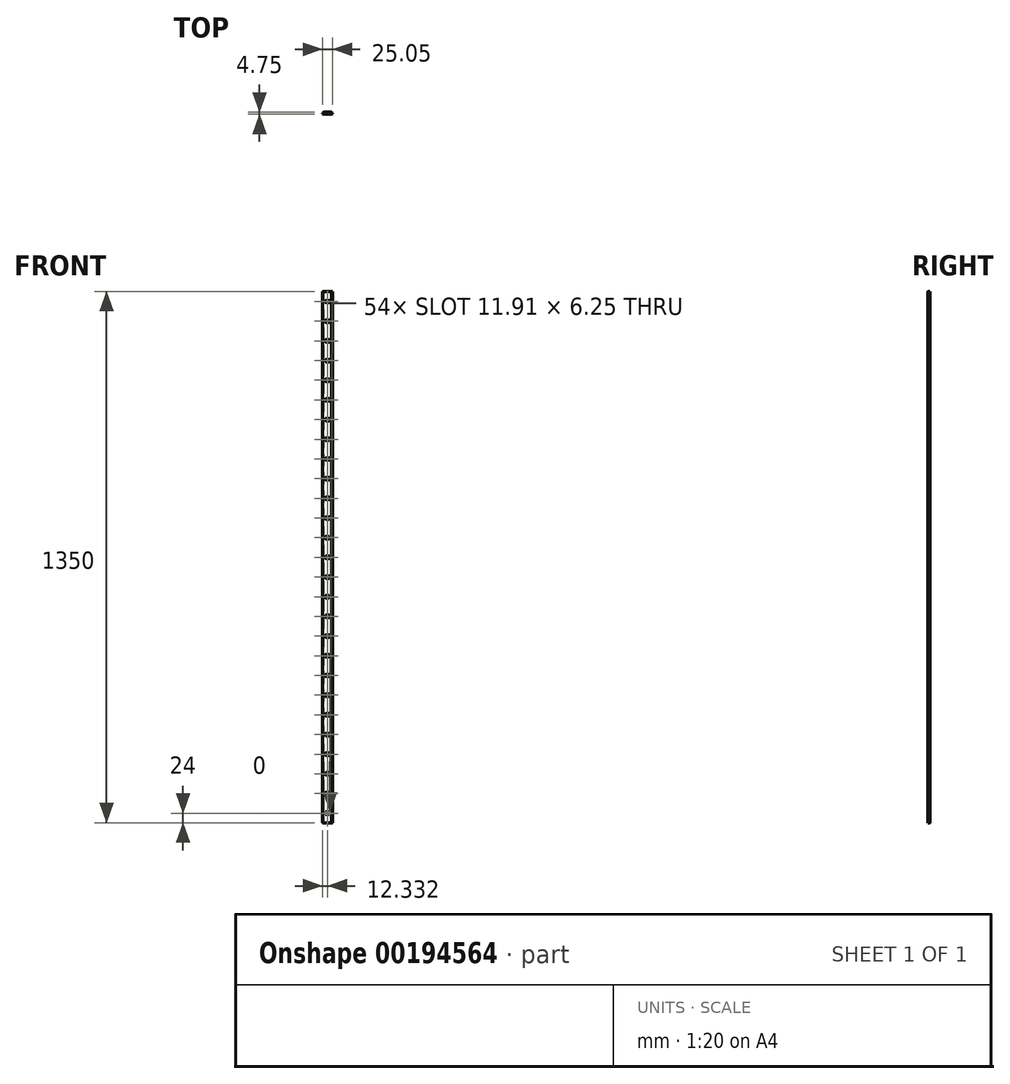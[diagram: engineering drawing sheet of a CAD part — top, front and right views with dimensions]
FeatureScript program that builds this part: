
annotation { "Feature Type Name" : "Feature", "Feature Type Description" : "" }
export const myFeature = defineFeature(function(context is Context, id is Id, definition is map)
    precondition{}
    {
        {
            var Q0;
            Q0=qCreatedBy(makeId("Top.planeOp"),FACE);
            var sketch = newSketch(context, id + "F0", { "sketchPlane" : qUnion([Q0])});
            skLineSegment(sketch, "E0", {"start": v(0, 0) * mm, "end": v(20.12, 0) * mm});
            skLineSegment(sketch, "E1", {"start": v(20.12, 0) * mm, "end": v(22.5, -2.37) * mm});
            skLineSegment(sketch, "E2", {"start": v(22.5, -2.37) * mm, "end": v(20.12, -4.75) * mm});
            skLineSegment(sketch, "E3", {"start": v(20.12, -4.75) * mm, "end": v(19.53, -4.75) * mm});
            skLineSegment(sketch, "E4", {"start": v(19.53, -4.75) * mm, "end": v(19.53, -2.37) * mm});
            skLineSegment(sketch, "E5", {"start": v(19.53, -2.37) * mm, "end": v(0, -2.38) * mm});
            skLineSegment(sketch, "E6", {"start": v(0, -2.38) * mm, "end": v(0, 0) * mm});
            skSolve(sketch);
        }
        {
            var Q0;
            Q0 = qSketchRegion(id + "F0", true);
            extrude(context, id + "F1", {"entities" : qUnion([Q0]), "depth" : 1350 * mm});
        }
        {
            var Q0;
            Q0=makeQuery(id+"F1.opExtrude","SWEPT_EDGE",EDGE,{"disambiguationData":[OSD([sQuery(id+"F0.wireOp",EDGE,"E2"),sQuery(id+"F0.wireOp",EDGE,"E3")])]});
            var Q1;
            Q1=makeQuery(id+"F1.opExtrude","SWEPT_EDGE",EDGE,{"disambiguationData":[OSD([sQuery(id+"F0.wireOp",EDGE,"E1"),sQuery(id+"F0.wireOp",EDGE,"E2")])]});
            var Q2;
            Q2=makeQuery(id+"F1.opExtrude","SWEPT_EDGE",EDGE,{"disambiguationData":[OSD([sQuery(id+"F0.wireOp",EDGE,"E0"),sQuery(id+"F0.wireOp",EDGE,"E1")])]});
            fillet(context, id + "F2", {"entities" : qUnion([Q0, Q1, Q2]), "radius" : 0.5 * mm, "tangentPropagation" : true, "allowEdgeOverflow" : false});
        }
        {
            var Q0;
            Q0=makeQuery(id+"F1.opExtrude","SWEPT_BODY",BODY,{"disambiguationData":[OSD([sQuery(id+"F0.wireOp",EDGE,"E0"),sQuery(id+"F0.wireOp",EDGE,"E1"),sQuery(id+"F0.wireOp",EDGE,"E2"),sQuery(id+"F0.wireOp",EDGE,"E3"),sQuery(id+"F0.wireOp",EDGE,"E4"),sQuery(id+"F0.wireOp",EDGE,"E5"),sQuery(id+"F0.wireOp",EDGE,"E6")])]});
            var Q1;
            Q1=makeQuery(id+"F1.opExtrude","SWEPT_EDGE",EDGE,{"disambiguationData":[OSD([sQuery(id+"F0.wireOp",EDGE,"E5"),sQuery(id+"F0.wireOp",EDGE,"E6")])]});
            transform(context, id + "F3", {"entities" : qUnion([Q0]), "transformType" : TransformType.ROTATION, "transformAxis" : qUnion([Q1]), "angle" : 180 * degree, "makeCopy" : true});
        }
        {
            var Q0;
            Q0=makeQuery(id+"F3.opPattern","COPY",BODY,{"derivedFrom":makeQuery(id+"F1.opExtrude","SWEPT_BODY",BODY,{"disambiguationData":[OSD([sQuery(id+"F0.wireOp",EDGE,"E0"),sQuery(id+"F0.wireOp",EDGE,"E1"),sQuery(id+"F0.wireOp",EDGE,"E2"),sQuery(id+"F0.wireOp",EDGE,"E3"),sQuery(id+"F0.wireOp",EDGE,"E4"),sQuery(id+"F0.wireOp",EDGE,"E5"),sQuery(id+"F0.wireOp",EDGE,"E6")])]}),"instanceName":"1"});
            var Q1;
            Q1=makeQuery(id+"F3.opPattern","COPY",EDGE,{"derivedFrom":makeQuery(id+"F1.opExtrude","CAP_EDGE",EDGE,{"disambiguationData":[OSD([sQuery(id+"F0.wireOp",EDGE,"E5")])],"isStart":true}),"instanceName":"1"});
            transform(context, id + "F4", {"entities" : qUnion([Q0]), "transformType" : TransformType.TRANSLATION_ENTITY, "oppositeDirectionEntity" : false, "transformLine" : qUnion([Q1]), "makeCopy" : false});
        }
        {
            var Q0;
            Q0=makeQuery(id+"F3.opPattern","COPY",FACE,{"derivedFrom":makeQuery(id+"F1.opExtrude","SWEPT_FACE",FACE,{"disambiguationData":[OSD([sQuery(id+"F0.wireOp",EDGE,"E0")])]}),"instanceName":"1"});
            var sketch = newSketch(context, id + "F5", { "sketchPlane" : qUnion([Q0])});
            skLineSegment(sketch, "E7", {"start": v(9.57, 1350) * mm, "end": v(9.57, 1284.45) * mm, "construction": true});
            skLineSegment(sketch, "E8", {"start": v(-9.43, 1324) * mm, "end": v(34.24, 1324) * mm, "construction": true});
            skArc(sketch, "E9", {"start": v(9.57, 1322.68) * mm, "mid": v(15.04, 1322.32) * mm, "end": v(12.4, 1327.12) * mm});
            skArc(sketch, "E10", {"start": v(6.74, 1327.12) * mm, "mid": v(4.1, 1322.32) * mm, "end": v(9.57, 1322.68) * mm});
            skLineSegment(sketch, "E11", {"start": v(12.4, 1320.88) * mm, "end": v(6.74, 1320.88) * mm});
            skLineSegment(sketch, "E12", {"start": v(12.4, 1327.12) * mm, "end": v(6.74, 1327.12) * mm});
            skArc(sketch, "E13.0.1.0", {"start": v(6.74, 1277.12) * mm, "mid": v(4.1, 1272.32) * mm, "end": v(9.57, 1272.68) * mm});
            skLineSegment(sketch, "E13.0.1.1", {"start": v(12.4, 1270.88) * mm, "end": v(6.74, 1270.88) * mm});
            skArc(sketch, "E13.0.1.2", {"start": v(9.57, 1272.68) * mm, "mid": v(15.04, 1272.32) * mm, "end": v(12.4, 1277.12) * mm});
            skLineSegment(sketch, "E13.0.1.3", {"start": v(12.4, 1277.12) * mm, "end": v(6.74, 1277.12) * mm});
            skArc(sketch, "E13.0.2.0", {"start": v(6.74, 1227.13) * mm, "mid": v(4.1, 1222.32) * mm, "end": v(9.57, 1222.68) * mm});
            skLineSegment(sketch, "E13.0.2.1", {"start": v(12.4, 1220.88) * mm, "end": v(6.74, 1220.88) * mm});
            skArc(sketch, "E13.0.2.2", {"start": v(9.57, 1222.68) * mm, "mid": v(15.04, 1222.32) * mm, "end": v(12.4, 1227.13) * mm});
            skLineSegment(sketch, "E13.0.2.3", {"start": v(12.4, 1227.13) * mm, "end": v(6.74, 1227.13) * mm});
            skArc(sketch, "E13.0.3.0", {"start": v(6.74, 1177.13) * mm, "mid": v(4.1, 1172.32) * mm, "end": v(9.57, 1172.68) * mm});
            skLineSegment(sketch, "E13.0.3.1", {"start": v(12.4, 1170.88) * mm, "end": v(6.74, 1170.88) * mm});
            skArc(sketch, "E13.0.3.2", {"start": v(9.57, 1172.68) * mm, "mid": v(15.04, 1172.32) * mm, "end": v(12.4, 1177.13) * mm});
            skLineSegment(sketch, "E13.0.3.3", {"start": v(12.4, 1177.13) * mm, "end": v(6.74, 1177.13) * mm});
            skArc(sketch, "E13.0.4.0", {"start": v(6.74, 1127.13) * mm, "mid": v(4.1, 1122.32) * mm, "end": v(9.57, 1122.68) * mm});
            skLineSegment(sketch, "E13.0.4.1", {"start": v(12.4, 1120.88) * mm, "end": v(6.74, 1120.88) * mm});
            skArc(sketch, "E13.0.4.2", {"start": v(9.57, 1122.68) * mm, "mid": v(15.04, 1122.32) * mm, "end": v(12.4, 1127.13) * mm});
            skLineSegment(sketch, "E13.0.4.3", {"start": v(12.4, 1127.13) * mm, "end": v(6.74, 1127.13) * mm});
            skArc(sketch, "E13.0.5.0", {"start": v(6.74, 1077.13) * mm, "mid": v(4.1, 1072.32) * mm, "end": v(9.57, 1072.68) * mm});
            skLineSegment(sketch, "E13.0.5.1", {"start": v(12.4, 1070.88) * mm, "end": v(6.74, 1070.88) * mm});
            skArc(sketch, "E13.0.5.2", {"start": v(9.57, 1072.68) * mm, "mid": v(15.04, 1072.32) * mm, "end": v(12.4, 1077.13) * mm});
            skLineSegment(sketch, "E13.0.5.3", {"start": v(12.4, 1077.13) * mm, "end": v(6.74, 1077.13) * mm});
            skArc(sketch, "E13.0.6.0", {"start": v(6.74, 1027.13) * mm, "mid": v(4.1, 1022.32) * mm, "end": v(9.57, 1022.68) * mm});
            skLineSegment(sketch, "E13.0.6.1", {"start": v(12.4, 1020.88) * mm, "end": v(6.74, 1020.88) * mm});
            skArc(sketch, "E13.0.6.2", {"start": v(9.57, 1022.68) * mm, "mid": v(15.04, 1022.32) * mm, "end": v(12.4, 1027.13) * mm});
            skLineSegment(sketch, "E13.0.6.3", {"start": v(12.4, 1027.13) * mm, "end": v(6.74, 1027.13) * mm});
            skArc(sketch, "E13.0.7.0", {"start": v(6.74, 977.13) * mm, "mid": v(4.1, 972.32) * mm, "end": v(9.57, 972.68) * mm});
            skLineSegment(sketch, "E13.0.7.1", {"start": v(12.4, 970.88) * mm, "end": v(6.74, 970.88) * mm});
            skArc(sketch, "E13.0.7.2", {"start": v(9.57, 972.68) * mm, "mid": v(15.04, 972.32) * mm, "end": v(12.4, 977.13) * mm});
            skLineSegment(sketch, "E13.0.7.3", {"start": v(12.4, 977.13) * mm, "end": v(6.74, 977.13) * mm});
            skArc(sketch, "E13.0.8.0", {"start": v(6.74, 927.13) * mm, "mid": v(4.1, 922.32) * mm, "end": v(9.57, 922.68) * mm});
            skLineSegment(sketch, "E13.0.8.1", {"start": v(12.4, 920.88) * mm, "end": v(6.74, 920.88) * mm});
            skArc(sketch, "E13.0.8.2", {"start": v(9.57, 922.68) * mm, "mid": v(15.04, 922.32) * mm, "end": v(12.4, 927.13) * mm});
            skLineSegment(sketch, "E13.0.8.3", {"start": v(12.4, 927.13) * mm, "end": v(6.74, 927.13) * mm});
            skArc(sketch, "E13.0.9.0", {"start": v(6.74, 877.13) * mm, "mid": v(4.1, 872.32) * mm, "end": v(9.57, 872.68) * mm});
            skLineSegment(sketch, "E13.0.9.1", {"start": v(12.4, 870.88) * mm, "end": v(6.74, 870.88) * mm});
            skArc(sketch, "E13.0.9.2", {"start": v(9.57, 872.68) * mm, "mid": v(15.04, 872.32) * mm, "end": v(12.4, 877.13) * mm});
            skLineSegment(sketch, "E13.0.9.3", {"start": v(12.4, 877.13) * mm, "end": v(6.74, 877.13) * mm});
            skArc(sketch, "E13.0.10.0", {"start": v(6.74, 827.13) * mm, "mid": v(4.1, 822.32) * mm, "end": v(9.57, 822.68) * mm});
            skLineSegment(sketch, "E13.0.10.1", {"start": v(12.4, 820.88) * mm, "end": v(6.74, 820.88) * mm});
            skArc(sketch, "E13.0.10.2", {"start": v(9.57, 822.68) * mm, "mid": v(15.04, 822.32) * mm, "end": v(12.4, 827.13) * mm});
            skLineSegment(sketch, "E13.0.10.3", {"start": v(12.4, 827.13) * mm, "end": v(6.74, 827.13) * mm});
            skArc(sketch, "E13.0.11.0", {"start": v(6.74, 777.13) * mm, "mid": v(4.1, 772.32) * mm, "end": v(9.57, 772.68) * mm});
            skLineSegment(sketch, "E13.0.11.1", {"start": v(12.4, 770.88) * mm, "end": v(6.74, 770.88) * mm});
            skArc(sketch, "E13.0.11.2", {"start": v(9.57, 772.68) * mm, "mid": v(15.04, 772.32) * mm, "end": v(12.4, 777.13) * mm});
            skLineSegment(sketch, "E13.0.11.3", {"start": v(12.4, 777.13) * mm, "end": v(6.74, 777.13) * mm});
            skArc(sketch, "E13.0.12.0", {"start": v(6.74, 727.13) * mm, "mid": v(4.1, 722.32) * mm, "end": v(9.57, 722.68) * mm});
            skLineSegment(sketch, "E13.0.12.1", {"start": v(12.4, 720.88) * mm, "end": v(6.74, 720.88) * mm});
            skArc(sketch, "E13.0.12.2", {"start": v(9.57, 722.68) * mm, "mid": v(15.04, 722.32) * mm, "end": v(12.4, 727.13) * mm});
            skLineSegment(sketch, "E13.0.12.3", {"start": v(12.4, 727.13) * mm, "end": v(6.74, 727.13) * mm});
            skArc(sketch, "E13.0.13.0", {"start": v(6.74, 677.13) * mm, "mid": v(4.1, 672.32) * mm, "end": v(9.57, 672.68) * mm});
            skLineSegment(sketch, "E13.0.13.1", {"start": v(12.4, 670.88) * mm, "end": v(6.74, 670.88) * mm});
            skArc(sketch, "E13.0.13.2", {"start": v(9.57, 672.68) * mm, "mid": v(15.04, 672.32) * mm, "end": v(12.4, 677.13) * mm});
            skLineSegment(sketch, "E13.0.13.3", {"start": v(12.4, 677.13) * mm, "end": v(6.74, 677.13) * mm});
            skArc(sketch, "E13.0.14.0", {"start": v(6.74, 627.13) * mm, "mid": v(4.1, 622.32) * mm, "end": v(9.57, 622.68) * mm});
            skLineSegment(sketch, "E13.0.14.1", {"start": v(12.4, 620.88) * mm, "end": v(6.74, 620.88) * mm});
            skArc(sketch, "E13.0.14.2", {"start": v(9.57, 622.68) * mm, "mid": v(15.04, 622.32) * mm, "end": v(12.4, 627.13) * mm});
            skLineSegment(sketch, "E13.0.14.3", {"start": v(12.4, 627.13) * mm, "end": v(6.74, 627.13) * mm});
            skArc(sketch, "E13.0.15.0", {"start": v(6.74, 577.13) * mm, "mid": v(4.1, 572.32) * mm, "end": v(9.57, 572.68) * mm});
            skLineSegment(sketch, "E13.0.15.1", {"start": v(12.4, 570.88) * mm, "end": v(6.74, 570.88) * mm});
            skArc(sketch, "E13.0.15.2", {"start": v(9.57, 572.68) * mm, "mid": v(15.04, 572.32) * mm, "end": v(12.4, 577.13) * mm});
            skLineSegment(sketch, "E13.0.15.3", {"start": v(12.4, 577.13) * mm, "end": v(6.74, 577.13) * mm});
            skArc(sketch, "E13.0.16.0", {"start": v(6.74, 527.13) * mm, "mid": v(4.1, 522.32) * mm, "end": v(9.57, 522.68) * mm});
            skLineSegment(sketch, "E13.0.16.1", {"start": v(12.4, 520.88) * mm, "end": v(6.74, 520.88) * mm});
            skArc(sketch, "E13.0.16.2", {"start": v(9.57, 522.68) * mm, "mid": v(15.04, 522.32) * mm, "end": v(12.4, 527.13) * mm});
            skLineSegment(sketch, "E13.0.16.3", {"start": v(12.4, 527.13) * mm, "end": v(6.74, 527.13) * mm});
            skArc(sketch, "E13.0.17.0", {"start": v(6.74, 477.13) * mm, "mid": v(4.1, 472.32) * mm, "end": v(9.57, 472.68) * mm});
            skLineSegment(sketch, "E13.0.17.1", {"start": v(12.4, 470.88) * mm, "end": v(6.74, 470.88) * mm});
            skArc(sketch, "E13.0.17.2", {"start": v(9.57, 472.68) * mm, "mid": v(15.04, 472.32) * mm, "end": v(12.4, 477.13) * mm});
            skLineSegment(sketch, "E13.0.17.3", {"start": v(12.4, 477.13) * mm, "end": v(6.74, 477.13) * mm});
            skArc(sketch, "E13.0.18.0", {"start": v(6.74, 427.13) * mm, "mid": v(4.1, 422.32) * mm, "end": v(9.57, 422.68) * mm});
            skLineSegment(sketch, "E13.0.18.1", {"start": v(12.4, 420.88) * mm, "end": v(6.74, 420.88) * mm});
            skArc(sketch, "E13.0.18.2", {"start": v(9.57, 422.68) * mm, "mid": v(15.04, 422.32) * mm, "end": v(12.4, 427.13) * mm});
            skLineSegment(sketch, "E13.0.18.3", {"start": v(12.4, 427.13) * mm, "end": v(6.74, 427.13) * mm});
            skArc(sketch, "E13.0.19.0", {"start": v(6.74, 377.13) * mm, "mid": v(4.1, 372.32) * mm, "end": v(9.57, 372.68) * mm});
            skLineSegment(sketch, "E13.0.19.1", {"start": v(12.4, 370.88) * mm, "end": v(6.74, 370.88) * mm});
            skArc(sketch, "E13.0.19.2", {"start": v(9.57, 372.68) * mm, "mid": v(15.04, 372.32) * mm, "end": v(12.4, 377.13) * mm});
            skLineSegment(sketch, "E13.0.19.3", {"start": v(12.4, 377.13) * mm, "end": v(6.74, 377.13) * mm});
            skLineSegment(sketch, "E13.direction1", {"start": v(6.74, 1320.88) * mm, "end": v(-20.5, 1325.4) * mm, "construction": true});
            skLineSegment(sketch, "E13.direction2", {"start": v(6.74, 1320.88) * mm, "end": v(6.74, 1270.88) * mm, "construction": true});
            skArc(sketch, "E14.0.0.20", {"start": v(6.74, 327.13) * mm, "mid": v(4.1, 322.32) * mm, "end": v(9.57, 322.68) * mm});
            skLineSegment(sketch, "E14.4.0.20", {"start": v(12.4, 320.88) * mm, "end": v(6.74, 320.88) * mm});
            skArc(sketch, "E14.7.0.20", {"start": v(9.57, 322.68) * mm, "mid": v(15.04, 322.32) * mm, "end": v(12.4, 327.13) * mm});
            skLineSegment(sketch, "E14.11.0.20", {"start": v(12.4, 327.13) * mm, "end": v(6.74, 327.13) * mm});
            skArc(sketch, "E14.0.0.21", {"start": v(6.74, 277.13) * mm, "mid": v(4.1, 272.32) * mm, "end": v(9.57, 272.68) * mm});
            skLineSegment(sketch, "E14.4.0.21", {"start": v(12.4, 270.88) * mm, "end": v(6.74, 270.88) * mm});
            skArc(sketch, "E14.7.0.21", {"start": v(9.57, 272.68) * mm, "mid": v(15.04, 272.32) * mm, "end": v(12.4, 277.13) * mm});
            skLineSegment(sketch, "E14.11.0.21", {"start": v(12.4, 277.13) * mm, "end": v(6.74, 277.13) * mm});
            skArc(sketch, "E14.0.0.22", {"start": v(6.74, 227.13) * mm, "mid": v(4.1, 222.32) * mm, "end": v(9.57, 222.68) * mm});
            skLineSegment(sketch, "E14.4.0.22", {"start": v(12.4, 220.88) * mm, "end": v(6.74, 220.88) * mm});
            skArc(sketch, "E14.7.0.22", {"start": v(9.57, 222.68) * mm, "mid": v(15.04, 222.32) * mm, "end": v(12.4, 227.13) * mm});
            skLineSegment(sketch, "E14.11.0.22", {"start": v(12.4, 227.13) * mm, "end": v(6.74, 227.13) * mm});
            skArc(sketch, "E14.0.0.23", {"start": v(6.74, 177.13) * mm, "mid": v(4.1, 172.32) * mm, "end": v(9.57, 172.68) * mm});
            skLineSegment(sketch, "E14.4.0.23", {"start": v(12.4, 170.88) * mm, "end": v(6.74, 170.88) * mm});
            skArc(sketch, "E14.7.0.23", {"start": v(9.57, 172.68) * mm, "mid": v(15.04, 172.32) * mm, "end": v(12.4, 177.13) * mm});
            skLineSegment(sketch, "E14.11.0.23", {"start": v(12.4, 177.13) * mm, "end": v(6.74, 177.13) * mm});
            skArc(sketch, "E14.0.0.24", {"start": v(6.74, 127.13) * mm, "mid": v(4.1, 122.32) * mm, "end": v(9.57, 122.68) * mm});
            skLineSegment(sketch, "E14.4.0.24", {"start": v(12.4, 120.88) * mm, "end": v(6.74, 120.88) * mm});
            skArc(sketch, "E14.7.0.24", {"start": v(9.57, 122.68) * mm, "mid": v(15.04, 122.32) * mm, "end": v(12.4, 127.13) * mm});
            skLineSegment(sketch, "E14.11.0.24", {"start": v(12.4, 127.13) * mm, "end": v(6.74, 127.13) * mm});
            skArc(sketch, "E14.0.0.25", {"start": v(6.74, 77.13) * mm, "mid": v(4.1, 72.32) * mm, "end": v(9.57, 72.68) * mm});
            skLineSegment(sketch, "E14.4.0.25", {"start": v(12.4, 70.88) * mm, "end": v(6.74, 70.88) * mm});
            skArc(sketch, "E14.7.0.25", {"start": v(9.57, 72.68) * mm, "mid": v(15.04, 72.32) * mm, "end": v(12.4, 77.13) * mm});
            skLineSegment(sketch, "E14.11.0.25", {"start": v(12.4, 77.13) * mm, "end": v(6.74, 77.13) * mm});
            skArc(sketch, "E14.0.0.26", {"start": v(6.74, 27.13) * mm, "mid": v(4.1, 22.32) * mm, "end": v(9.57, 22.68) * mm});
            skLineSegment(sketch, "E14.4.0.26", {"start": v(12.4, 20.88) * mm, "end": v(6.74, 20.88) * mm});
            skArc(sketch, "E14.7.0.26", {"start": v(9.57, 22.68) * mm, "mid": v(15.04, 22.32) * mm, "end": v(12.4, 27.13) * mm});
            skLineSegment(sketch, "E14.11.0.26", {"start": v(12.4, 27.13) * mm, "end": v(6.74, 27.13) * mm});
            skArc(sketch, "E14.0.0.27", {"start": v(6.74, -22.87) * mm, "mid": v(4.1, -27.68) * mm, "end": v(9.57, -27.32) * mm});
            skLineSegment(sketch, "E14.4.0.27", {"start": v(12.4, -29.12) * mm, "end": v(6.74, -29.12) * mm});
            skArc(sketch, "E14.7.0.27", {"start": v(9.57, -27.32) * mm, "mid": v(15.04, -27.68) * mm, "end": v(12.4, -22.87) * mm});
            skLineSegment(sketch, "E14.11.0.27", {"start": v(12.4, -22.87) * mm, "end": v(6.74, -22.87) * mm});
            skArc(sketch, "E14.0.0.28", {"start": v(6.74, -72.87) * mm, "mid": v(4.1, -77.68) * mm, "end": v(9.57, -77.32) * mm});
            skLineSegment(sketch, "E14.4.0.28", {"start": v(12.4, -79.12) * mm, "end": v(6.74, -79.12) * mm});
            skArc(sketch, "E14.7.0.28", {"start": v(9.57, -77.32) * mm, "mid": v(15.04, -77.68) * mm, "end": v(12.4, -72.87) * mm});
            skLineSegment(sketch, "E14.11.0.28", {"start": v(12.4, -72.87) * mm, "end": v(6.74, -72.87) * mm});
            skArc(sketch, "E14.0.0.29", {"start": v(6.74, -122.87) * mm, "mid": v(4.1, -127.68) * mm, "end": v(9.57, -127.32) * mm});
            skLineSegment(sketch, "E14.4.0.29", {"start": v(12.4, -129.12) * mm, "end": v(6.74, -129.12) * mm});
            skArc(sketch, "E14.7.0.29", {"start": v(9.57, -127.32) * mm, "mid": v(15.04, -127.68) * mm, "end": v(12.4, -122.87) * mm});
            skLineSegment(sketch, "E14.11.0.29", {"start": v(12.4, -122.87) * mm, "end": v(6.74, -122.87) * mm});
            skSolve(sketch);
        }
        {
            var Q0;
            Q0 = qSketchRegion(id + "F5", true);
            extrude(context, id + "F6", {"entities" : qUnion([Q0]), "operationType" : NewBodyOperationType.REMOVE, "oppositeDirection" : true, "depth" : 25 * mm});
        }
    });
